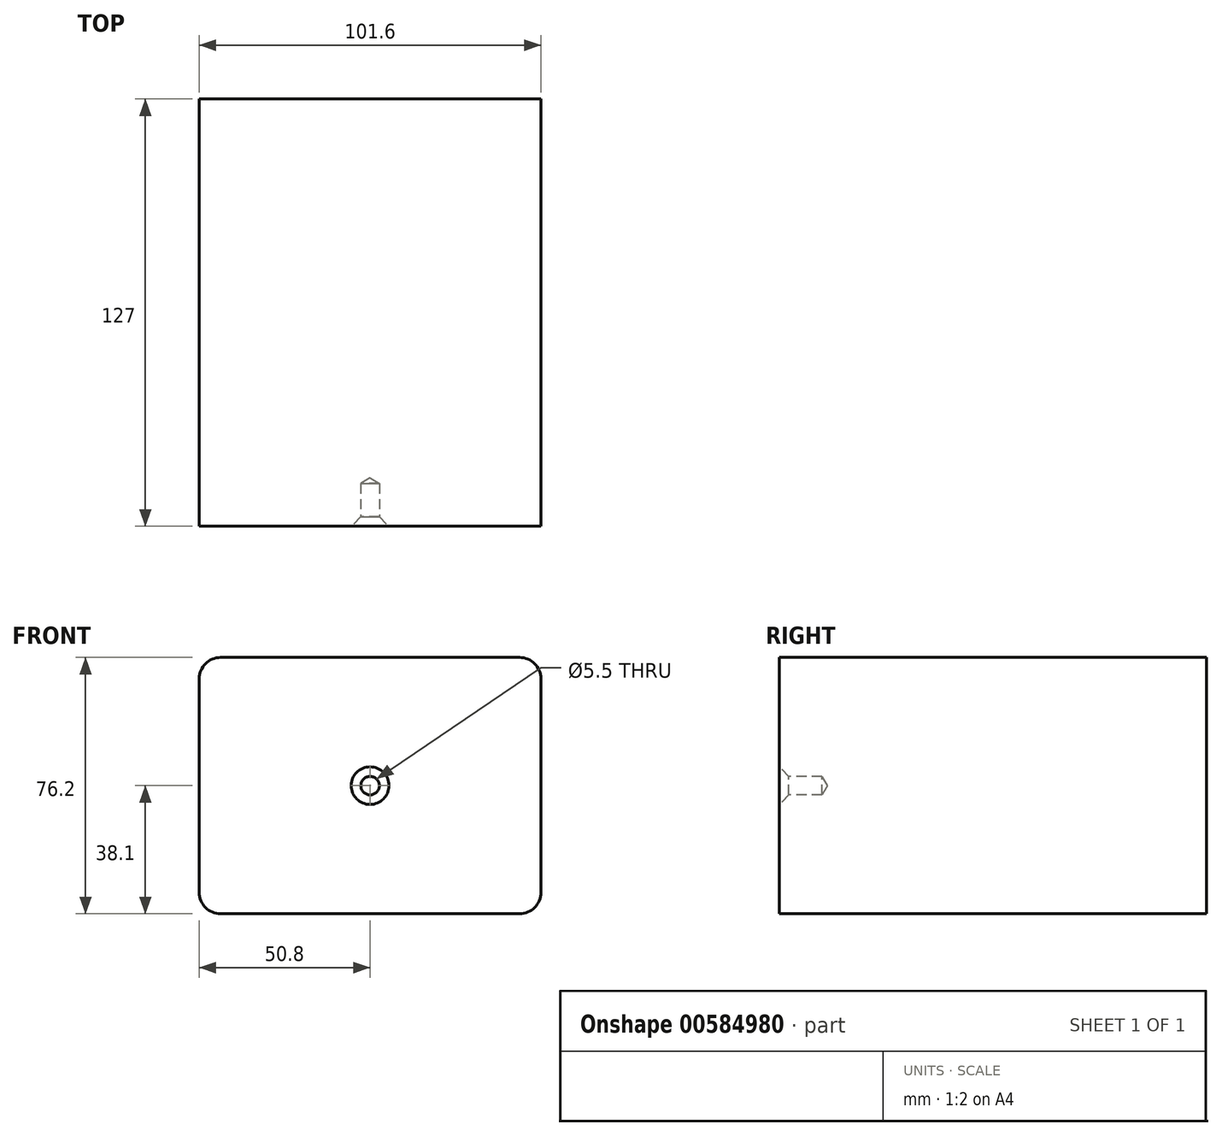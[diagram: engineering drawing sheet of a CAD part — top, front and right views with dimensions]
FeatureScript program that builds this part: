
annotation { "Feature Type Name" : "Feature", "Feature Type Description" : "" }
export const myFeature = defineFeature(function(context is Context, id is Id, definition is map)
    precondition{}
    {
        {
            var Q0;
            Q0=qCreatedBy(makeId("Front.planeOp"),FACE);
            var sketch = newSketch(context, id + "F0", { "sketchPlane" : qUnion([Q0])});
            skLineSegment(sketch, "E0.bottom", {"start": v(-44.45, -38.1) * mm, "end": v(44.45, -38.1) * mm});
            skLineSegment(sketch, "E0.top", {"start": v(-44.45, 38.1) * mm, "end": v(44.45, 38.1) * mm});
            skLineSegment(sketch, "E0.left", {"start": v(-50.8, -31.75) * mm, "end": v(-50.8, 31.75) * mm});
            skLineSegment(sketch, "E0.right", {"start": v(50.8, -31.75) * mm, "end": v(50.8, 31.75) * mm});
            skPoint(sketch, "E0.middle", {"position": v(0, 0) * mm});
            skPoint(sketch, "E1.visualSharp", {"position": v(-50.8, 38.1) * mm});
            skArc(sketch, "E1.filletArc", {"start": v(-44.45, 38.1) * mm, "mid": v(-48.94, 36.24) * mm, "end": v(-50.8, 31.75) * mm});
            skPoint(sketch, "E2.visualSharp", {"position": v(50.8, 38.1) * mm});
            skArc(sketch, "E2.filletArc", {"start": v(50.8, 31.75) * mm, "mid": v(48.94, 36.24) * mm, "end": v(44.45, 38.1) * mm});
            skPoint(sketch, "E3.visualSharp", {"position": v(50.8, -38.1) * mm});
            skArc(sketch, "E3.filletArc", {"start": v(44.45, -38.1) * mm, "mid": v(48.94, -36.24) * mm, "end": v(50.8, -31.75) * mm});
            skPoint(sketch, "E4.visualSharp", {"position": v(-50.8, -38.1) * mm});
            skArc(sketch, "E4.filletArc", {"start": v(-50.8, -31.75) * mm, "mid": v(-48.94, -36.24) * mm, "end": v(-44.45, -38.1) * mm});
            skSolve(sketch);
        }
        {
            var Q0;
            Q0=makeQuery(id+"F0.imprint","IMPRINT",FACE,{"disambiguationData":[TD([[makeQuery(id+"F0.imprint","IMPRINT",EDGE,{"derivedFrom":sQuery(id+"F0.wireOp",EDGE,"E0.bottom")}),1.0]])]});
            extrude(context, id + "F1", {"entities" : qUnion([Q0]), "depth" : 127 * mm, "offsetDistance" : 25.4 * mm});
        }
        {
            var Q0;
            Q0=makeQuery(id+"F1.opExtrude","CAP_FACE",FACE,{"disambiguationData":[OSD([sQuery(id+"F0.wireOp",EDGE,"E0.bottom"),sQuery(id+"F0.wireOp",EDGE,"E0.top"),sQuery(id+"F0.wireOp",EDGE,"E0.left"),sQuery(id+"F0.wireOp",EDGE,"E0.right"),sQuery(id+"F0.wireOp",EDGE,"E1.filletArc"),sQuery(id+"F0.wireOp",EDGE,"E2.filletArc"),sQuery(id+"F0.wireOp",EDGE,"E3.filletArc"),sQuery(id+"F0.wireOp",EDGE,"E4.filletArc")])],"isStart":false});
            var sketch = newSketch(context, id + "F2", { "sketchPlane" : qUnion([Q0])});
            skLineSegment(sketch, "E5", {"start": v(0, 38.1) * mm, "end": v(0, -38.1) * mm, "construction": true});
            skLineSegment(sketch, "E6", {"start": v(-50.8, 0) * mm, "end": v(50.8, 0) * mm, "construction": true});
            skCircle(sketch, "E7", {"center": v(0, 0) * mm, "radius": 25.4 * mm});
            skSolve(sketch);
        }
        {
            var Q0;
            Q0=sQuery(id+"F2.wireOp",VERTEX,"E7.center");
            var Q1;
            Q1=makeQuery(id+"F1.opExtrude","SWEPT_BODY",BODY,{"disambiguationData":[OSD([sQuery(id+"F0.wireOp",EDGE,"E0.bottom"),sQuery(id+"F0.wireOp",EDGE,"E0.top"),sQuery(id+"F0.wireOp",EDGE,"E0.left"),sQuery(id+"F0.wireOp",EDGE,"E0.right"),sQuery(id+"F0.wireOp",EDGE,"E1.filletArc"),sQuery(id+"F0.wireOp",EDGE,"E2.filletArc"),sQuery(id+"F0.wireOp",EDGE,"E3.filletArc"),sQuery(id+"F0.wireOp",EDGE,"E4.filletArc")])]});
            hole(context, id + "F3", {"style" : HoleStyle.C_SINK, "endStyle" : HoleEndStyle.BLIND, "standardTappedOrClearance" : lookupTablePath({ "standard" : "ISO", "fit" : "Normal", "size" : "M5", "type" : "Clearance" }), "standardBlindInLast" : lookupTablePath({ "fit" : "Standard", "standard" : "ISO", "size" : "M5", "type" : "Clearance" }), "holeDiameter" : 5.5 * mm, "cSinkDiameter" : 11.2 * mm, "cSinkAngle" : 90 * degree, "majorDiameter" : 6.35 * mm, "holeDepth" : 12.7 * mm, "isTappedThrough" : true, "tappedDepth" : 12.7 * mm, "tapClearance" : 3, "startFromSketch" : true, "locations" : qUnion([Q0]), "scope" : qUnion([Q1])});
        }
    });
